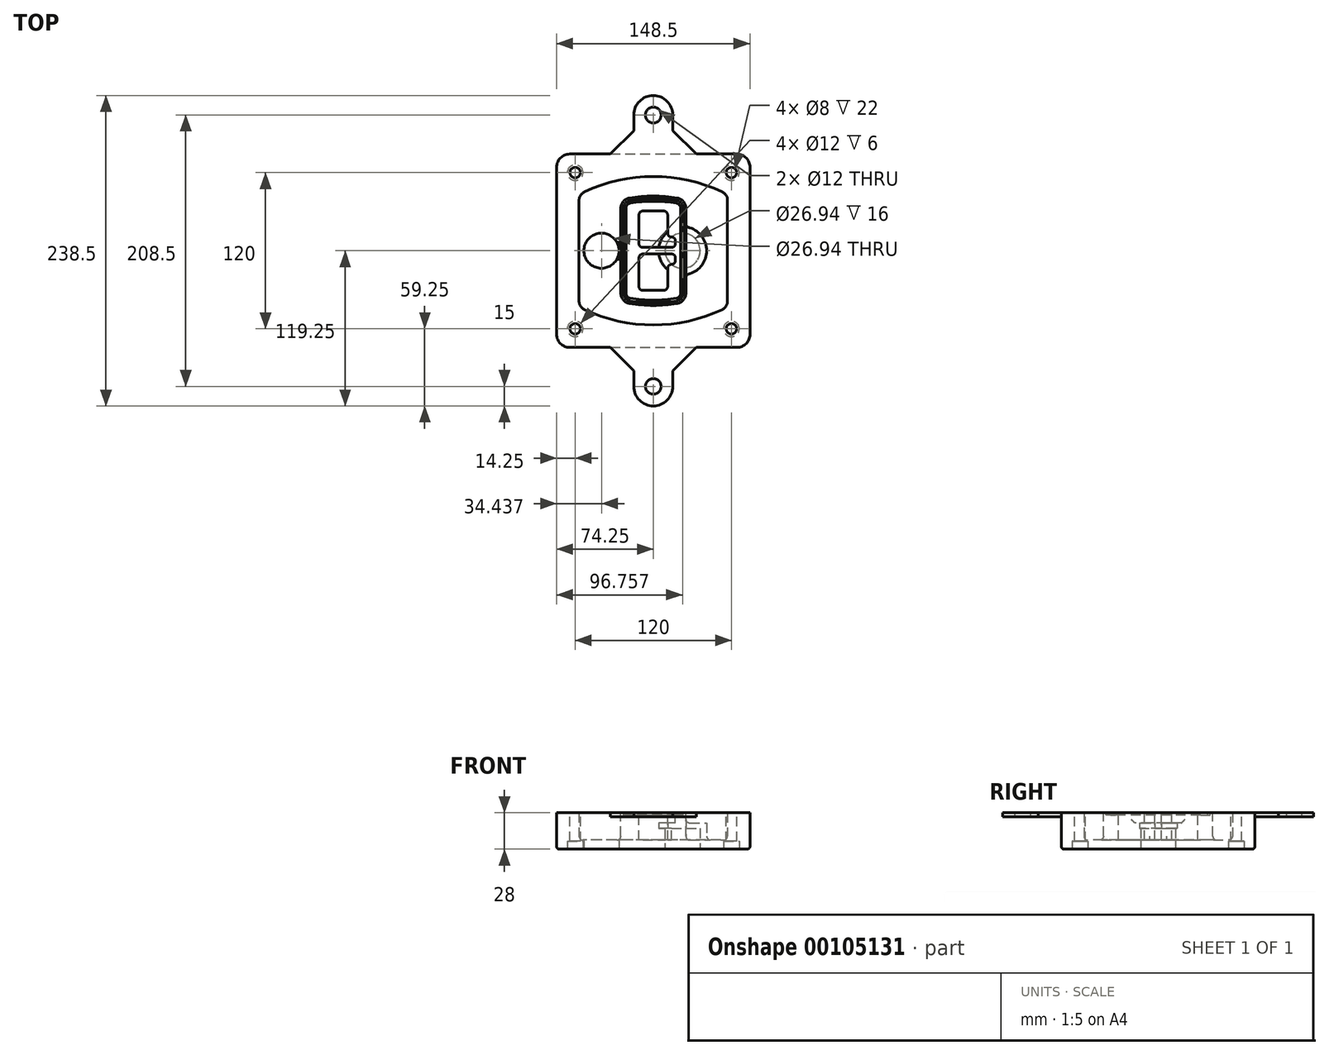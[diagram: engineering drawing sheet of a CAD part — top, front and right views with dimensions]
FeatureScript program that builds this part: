
annotation { "Feature Type Name" : "Feature", "Feature Type Description" : "" }
export const myFeature = defineFeature(function(context is Context, id is Id, definition is map)
    precondition{}
    {
        {
            var Q0;
            Q0=qCreatedBy(makeId("Top.planeOp"),FACE);
            var sketch = newSketch(context, id + "F0", { "sketchPlane" : qUnion([Q0])});
            skPoint(sketch, "E0.rect.middle", {"position": v(0, 0) * mm});
            skLineSegment(sketch, "E1.bottom", {"start": v(-64.25, -74.25) * mm, "end": v(64.25, -74.25) * mm});
            skLineSegment(sketch, "E1.top", {"start": v(-64.25, 74.25) * mm, "end": v(64.25, 74.25) * mm});
            skLineSegment(sketch, "E1.left", {"start": v(-74.25, -64.25) * mm, "end": v(-74.25, 64.25) * mm});
            skLineSegment(sketch, "E1.right", {"start": v(74.25, -64.25) * mm, "end": v(74.25, 64.25) * mm});
            skLineSegment(sketch, "E2", {"start": v(-74.25, 74.25) * mm, "end": v(74.25, -74.25) * mm, "construction": true});
            skLineSegment(sketch, "E3", {"start": v(74.25, 74.25) * mm, "end": v(-74.25, -74.25) * mm, "construction": true});
            skCircle(sketch, "E4", {"center": v(-60, 60) * mm, "radius": 4 * mm});
            skCircle(sketch, "E5", {"center": v(60, 60) * mm, "radius": 4 * mm});
            skCircle(sketch, "E6", {"center": v(60, -60) * mm, "radius": 4 * mm});
            skCircle(sketch, "E7", {"center": v(-60, -60) * mm, "radius": 4 * mm});
            skLineSegment(sketch, "E8", {"start": v(-60, 60) * mm, "end": v(60, 60) * mm, "construction": true});
            skLineSegment(sketch, "E9", {"start": v(60, 60) * mm, "end": v(60, -60) * mm, "construction": true});
            skLineSegment(sketch, "E10", {"start": v(60, -60) * mm, "end": v(-60, -60) * mm, "construction": true});
            skLineSegment(sketch, "E11", {"start": v(-60, -60) * mm, "end": v(-60, 60) * mm, "construction": true});
            skLineSegment(sketch, "E12", {"start": v(-60, 38.83) * mm, "end": v(-60, -38.83) * mm});
            skLineSegment(sketch, "E13", {"start": v(60, 38.83) * mm, "end": v(60, -38.83) * mm});
            skArc(sketch, "E14", {"start": v(54.26, 47.88) * mm, "mid": v(0, 60) * mm, "end": v(-54.26, 47.88) * mm});
            skArc(sketch, "E15", {"start": v(-54.26, -47.88) * mm, "mid": v(0, -60) * mm, "end": v(54.26, -47.88) * mm});
            skLineSegment(sketch, "E16", {"start": v(-60, 0) * mm, "end": v(60, 0) * mm, "construction": true});
            skPoint(sketch, "E17.visualSharp", {"position": v(-60, -45) * mm});
            skArc(sketch, "E17.filletArc", {"start": v(-60, -38.83) * mm, "mid": v(-58.44, -44.2) * mm, "end": v(-54.26, -47.88) * mm});
            skPoint(sketch, "E18.visualSharp", {"position": v(-60, 45) * mm});
            skArc(sketch, "E18.filletArc", {"start": v(-54.26, 47.88) * mm, "mid": v(-58.44, 44.2) * mm, "end": v(-60, 38.83) * mm});
            skPoint(sketch, "E19.visualSharp", {"position": v(60, 45) * mm});
            skArc(sketch, "E19.filletArc", {"start": v(60, 38.83) * mm, "mid": v(58.44, 44.2) * mm, "end": v(54.26, 47.88) * mm});
            skPoint(sketch, "E20.visualSharp", {"position": v(60, -45) * mm});
            skArc(sketch, "E20.filletArc", {"start": v(54.26, -47.88) * mm, "mid": v(58.44, -44.2) * mm, "end": v(60, -38.83) * mm});
            skPoint(sketch, "E21.visualSharp", {"position": v(-74.25, 74.25) * mm});
            skArc(sketch, "E21.filletArc", {"start": v(-64.25, 74.25) * mm, "mid": v(-71.32, 71.32) * mm, "end": v(-74.25, 64.25) * mm});
            skPoint(sketch, "E22.visualSharp", {"position": v(74.25, 74.25) * mm});
            skArc(sketch, "E22.filletArc", {"start": v(74.25, 64.25) * mm, "mid": v(71.32, 71.32) * mm, "end": v(64.25, 74.25) * mm});
            skPoint(sketch, "E23.visualSharp", {"position": v(74.25, -74.25) * mm});
            skArc(sketch, "E23.filletArc", {"start": v(64.25, -74.25) * mm, "mid": v(71.32, -71.32) * mm, "end": v(74.25, -64.25) * mm});
            skPoint(sketch, "E24.visualSharp", {"position": v(-74.25, -74.25) * mm});
            skArc(sketch, "E24.filletArc", {"start": v(-74.25, -64.25) * mm, "mid": v(-71.32, -71.32) * mm, "end": v(-64.25, -74.25) * mm});
            skArc(sketch, "E25.0", {"start": v(57, 38.83) * mm, "mid": v(55.9, 42.58) * mm, "end": v(52.98, 45.17) * mm});
            skLineSegment(sketch, "E25.1", {"start": v(57, 38.83) * mm, "end": v(57, -38.83) * mm});
            skArc(sketch, "E25.2", {"start": v(52.98, -45.17) * mm, "mid": v(55.9, -42.58) * mm, "end": v(57, -38.83) * mm});
            skArc(sketch, "E25.3", {"start": v(-52.98, -45.17) * mm, "mid": v(0, -57) * mm, "end": v(52.98, -45.17) * mm});
            skArc(sketch, "E25.4", {"start": v(-57, -38.83) * mm, "mid": v(-55.9, -42.58) * mm, "end": v(-52.98, -45.17) * mm});
            skArc(sketch, "E25.5", {"start": v(52.98, 45.17) * mm, "mid": v(0, 57) * mm, "end": v(-52.98, 45.17) * mm});
            skLineSegment(sketch, "E25.6", {"start": v(-57, 38.83) * mm, "end": v(-57, -38.83) * mm});
            skArc(sketch, "E25.7", {"start": v(-52.98, 45.17) * mm, "mid": v(-55.9, 42.58) * mm, "end": v(-57, 38.83) * mm});
            skArc(sketch, "E26.0", {"start": v(-55.96, 51.5) * mm, "mid": v(-61.82, 46.33) * mm, "end": v(-64, 38.83) * mm});
            skArc(sketch, "E26.1", {"start": v(55.96, 51.5) * mm, "mid": v(0, 64) * mm, "end": v(-55.96, 51.5) * mm});
            skArc(sketch, "E26.2", {"start": v(64, 38.83) * mm, "mid": v(61.82, 46.33) * mm, "end": v(55.96, 51.5) * mm});
            skLineSegment(sketch, "E26.3", {"start": v(64, 38.83) * mm, "end": v(64, -38.83) * mm});
            skArc(sketch, "E26.4", {"start": v(55.96, -51.5) * mm, "mid": v(61.82, -46.33) * mm, "end": v(64, -38.83) * mm});
            skLineSegment(sketch, "E26.5", {"start": v(-64, 38.83) * mm, "end": v(-64, -38.83) * mm});
            skArc(sketch, "E26.6", {"start": v(-55.96, -51.5) * mm, "mid": v(0, -64) * mm, "end": v(55.96, -51.5) * mm});
            skArc(sketch, "E26.7", {"start": v(-64, -38.83) * mm, "mid": v(-61.82, -46.33) * mm, "end": v(-55.96, -51.5) * mm});
            skSolve(sketch);
        }
        {
            var Q0;
            Q0=makeQuery(id+"F0.imprint","IMPRINT",FACE,{"disambiguationData":[TD([[makeQuery(id+"F0.imprint","IMPRINT",EDGE,{"derivedFrom":sQuery(id+"F0.wireOp",EDGE,"E1.bottom")}),1.0]])]});
            var Q1;
            Q1=makeQuery(id+"F0.imprint","IMPRINT",FACE,{"disambiguationData":[TD([[makeQuery(id+"F0.imprint","IMPRINT",EDGE,{"derivedFrom":sQuery(id+"F0.wireOp",EDGE,"E12")}),1.0]])]});
            var Q2;
            Q2=makeQuery(id+"F0.imprint","IMPRINT",FACE,{"disambiguationData":[TD([[makeQuery(id+"F0.imprint","IMPRINT",EDGE,{"derivedFrom":sQuery(id+"F0.wireOp",EDGE,"E25.0")}),1.0]])]});
            var Q3;
            Q3=makeQuery(id+"F0.imprint","IMPRINT",FACE,{"disambiguationData":[TD([[makeQuery(id+"F0.imprint","IMPRINT",EDGE,{"derivedFrom":sQuery(id+"F0.wireOp",EDGE,"E12")}),-1.0]])]});
            extrude(context, id + "F1", {"entities" : qUnion([Q0, Q1, Q2, Q3]), "oppositeDirection" : true, "depth" : 25 * mm});
        }
        {
            var Q0;
            Q0=makeQuery(id+"F0.imprint","IMPRINT",FACE,{"disambiguationData":[TD([[makeQuery(id+"F0.imprint","IMPRINT",EDGE,{"derivedFrom":sQuery(id+"F0.wireOp",EDGE,"E12")}),1.0]])]});
            extrude(context, id + "F2", {"entities" : qUnion([Q0]), "operationType" : NewBodyOperationType.ADD, "depth" : 3 * mm});
        }
        {
            var Q0;
            Q0=makeQuery(id+"F0.imprint","IMPRINT",FACE,{"disambiguationData":[TD([[makeQuery(id+"F0.imprint","IMPRINT",EDGE,{"derivedFrom":sQuery(id+"F0.wireOp",EDGE,"E25.0")}),1.0]])]});
            extrude(context, id + "F3", {"entities" : qUnion([Q0]), "operationType" : NewBodyOperationType.REMOVE, "oppositeDirection" : true, "depth" : 18 * mm});
        }
        {
            var Q0;
            Q0=makeQuery(id+"F2.opExtrude","CAP_FACE",FACE,{"disambiguationData":[OSD([sQuery(id+"F0.wireOp",EDGE,"E12"),sQuery(id+"F0.wireOp",EDGE,"E13"),sQuery(id+"F0.wireOp",EDGE,"E14"),sQuery(id+"F0.wireOp",EDGE,"E15"),sQuery(id+"F0.wireOp",EDGE,"E17.filletArc"),sQuery(id+"F0.wireOp",EDGE,"E18.filletArc"),sQuery(id+"F0.wireOp",EDGE,"E19.filletArc"),sQuery(id+"F0.wireOp",EDGE,"E20.filletArc"),sQuery(id+"F0.wireOp",EDGE,"E25.0"),sQuery(id+"F0.wireOp",EDGE,"E25.1"),sQuery(id+"F0.wireOp",EDGE,"E25.2"),sQuery(id+"F0.wireOp",EDGE,"E25.3"),sQuery(id+"F0.wireOp",EDGE,"E25.4"),sQuery(id+"F0.wireOp",EDGE,"E25.5"),sQuery(id+"F0.wireOp",EDGE,"E25.6"),sQuery(id+"F0.wireOp",EDGE,"E25.7")])],"isStart":false});
            var sketch = newSketch(context, id + "F4", { "sketchPlane" : qUnion([Q0])});
            skArc(sketch, "E27.0", {"start": v(-18.34, -40.45) * mm, "mid": v(0, -42) * mm, "end": v(18.34, -40.45) * mm});
            skArc(sketch, "E28.0", {"start": v(18.34, 40.45) * mm, "mid": v(0, 42) * mm, "end": v(-18.34, 40.45) * mm});
            skLineSegment(sketch, "E29", {"start": v(-25, 32.57) * mm, "end": v(-25, -32.57) * mm});
            skLineSegment(sketch, "E30", {"start": v(25, 32.57) * mm, "end": v(25, -32.57) * mm});
            skLineSegment(sketch, "E31", {"start": v(-25, 39.1) * mm, "end": v(25, 39.1) * mm, "construction": true});
            skLineSegment(sketch, "E32", {"start": v(-25, -39.1) * mm, "end": v(25, -39.1) * mm, "construction": true});
            skPoint(sketch, "E33.visualSharp", {"position": v(-25, 39.1) * mm});
            skArc(sketch, "E33.filletArc", {"start": v(-18.34, 40.45) * mm, "mid": v(-23.11, 37.73) * mm, "end": v(-25, 32.57) * mm});
            skPoint(sketch, "E34.visualSharp", {"position": v(25, 39.1) * mm});
            skArc(sketch, "E34.filletArc", {"start": v(25, 32.57) * mm, "mid": v(23.11, 37.73) * mm, "end": v(18.34, 40.45) * mm});
            skPoint(sketch, "E35.visualSharp", {"position": v(25, -39.1) * mm});
            skArc(sketch, "E35.filletArc", {"start": v(18.34, -40.45) * mm, "mid": v(23.11, -37.73) * mm, "end": v(25, -32.57) * mm});
            skPoint(sketch, "E36.visualSharp", {"position": v(-25, -39.1) * mm});
            skArc(sketch, "E36.filletArc", {"start": v(-25, -32.57) * mm, "mid": v(-23.11, -37.73) * mm, "end": v(-18.34, -40.45) * mm});
            skArc(sketch, "E37.0", {"start": v(52.98, 45.17) * mm, "mid": v(0, 57) * mm, "end": v(-52.98, 45.17) * mm});
            skArc(sketch, "E37.1", {"start": v(-52.98, 45.17) * mm, "mid": v(-55.9, 42.58) * mm, "end": v(-57, 38.83) * mm});
            skLineSegment(sketch, "E37.2", {"start": v(-57, 38.83) * mm, "end": v(-57, -38.83) * mm});
            skArc(sketch, "E37.3", {"start": v(-57, -38.83) * mm, "mid": v(-55.9, -42.58) * mm, "end": v(-52.98, -45.17) * mm});
            skArc(sketch, "E37.4", {"start": v(-52.98, -45.17) * mm, "mid": v(0, -57) * mm, "end": v(52.98, -45.17) * mm});
            skArc(sketch, "E37.5", {"start": v(52.98, -45.17) * mm, "mid": v(55.9, -42.58) * mm, "end": v(57, -38.83) * mm});
            skLineSegment(sketch, "E37.6", {"start": v(57, 38.83) * mm, "end": v(57, -38.83) * mm});
            skArc(sketch, "E37.7", {"start": v(57, 38.83) * mm, "mid": v(55.9, 42.58) * mm, "end": v(52.98, 45.17) * mm});
            skLineSegment(sketch, "E38.0", {"start": v(23, 32.57) * mm, "end": v(23, -32.57) * mm});
            skArc(sketch, "E38.1", {"start": v(18, -38.48) * mm, "mid": v(21.58, -36.44) * mm, "end": v(23, -32.57) * mm});
            skArc(sketch, "E38.2", {"start": v(-18, -38.48) * mm, "mid": v(0, -40) * mm, "end": v(18, -38.48) * mm});
            skArc(sketch, "E38.3", {"start": v(-23, -32.57) * mm, "mid": v(-21.58, -36.44) * mm, "end": v(-18, -38.48) * mm});
            skLineSegment(sketch, "E38.4", {"start": v(-23, 32.57) * mm, "end": v(-23, -32.57) * mm});
            skArc(sketch, "E38.5", {"start": v(23, 32.57) * mm, "mid": v(21.58, 36.44) * mm, "end": v(18, 38.48) * mm});
            skArc(sketch, "E38.6", {"start": v(-18, 38.48) * mm, "mid": v(-21.58, 36.44) * mm, "end": v(-23, 32.57) * mm});
            skArc(sketch, "E38.7", {"start": v(18, 38.48) * mm, "mid": v(0, 40) * mm, "end": v(-18, 38.48) * mm});
            skArc(sketch, "E39.0", {"start": v(21, 32.57) * mm, "mid": v(20.06, 35.15) * mm, "end": v(17.67, 36.5) * mm});
            skLineSegment(sketch, "E39.1", {"start": v(21, 32.57) * mm, "end": v(21, -32.57) * mm});
            skArc(sketch, "E39.2", {"start": v(17.67, -36.5) * mm, "mid": v(20.06, -35.15) * mm, "end": v(21, -32.57) * mm});
            skArc(sketch, "E39.3", {"start": v(-17.67, -36.5) * mm, "mid": v(0, -38) * mm, "end": v(17.67, -36.5) * mm});
            skArc(sketch, "E39.4", {"start": v(-21, -32.57) * mm, "mid": v(-20.06, -35.15) * mm, "end": v(-17.67, -36.5) * mm});
            skArc(sketch, "E39.5", {"start": v(17.67, 36.5) * mm, "mid": v(0, 38) * mm, "end": v(-17.67, 36.5) * mm});
            skLineSegment(sketch, "E39.6", {"start": v(-21, 32.57) * mm, "end": v(-21, -32.57) * mm});
            skArc(sketch, "E39.7", {"start": v(-17.67, 36.5) * mm, "mid": v(-20.06, 35.15) * mm, "end": v(-21, 32.57) * mm});
            skLineSegment(sketch, "E40", {"start": v(-25, 0) * mm, "end": v(25, 0) * mm, "construction": true});
            skLineSegment(sketch, "E41", {"start": v(-11, 5.5) * mm, "end": v(-11, 27.5) * mm});
            skLineSegment(sketch, "E42", {"start": v(-8, 30.5) * mm, "end": v(8, 30.5) * mm});
            skLineSegment(sketch, "E43", {"start": v(11, 27.5) * mm, "end": v(11, 13.5) * mm});
            skLineSegment(sketch, "E44", {"start": v(14, 10.5) * mm, "end": v(14, 10.5) * mm});
            skLineSegment(sketch, "E45", {"start": v(17, 7.5) * mm, "end": v(17, 5.5) * mm});
            skLineSegment(sketch, "E46", {"start": v(14, 2.5) * mm, "end": v(-8, 2.5) * mm});
            skPoint(sketch, "E47.visualSharp", {"position": v(-11, 30.5) * mm});
            skArc(sketch, "E47.filletArc", {"start": v(-8, 30.5) * mm, "mid": v(-10.12, 29.62) * mm, "end": v(-11, 27.5) * mm});
            skPoint(sketch, "E48.visualSharp", {"position": v(11, 30.5) * mm});
            skArc(sketch, "E48.filletArc", {"start": v(11, 27.5) * mm, "mid": v(10.12, 29.62) * mm, "end": v(8, 30.5) * mm});
            skPoint(sketch, "E49.visualSharp", {"position": v(11, 10.5) * mm});
            skArc(sketch, "E49.filletArc", {"start": v(11, 13.5) * mm, "mid": v(11.88, 11.38) * mm, "end": v(14, 10.5) * mm});
            skPoint(sketch, "E50.visualSharp", {"position": v(17, 10.5) * mm});
            skArc(sketch, "E50.filletArc", {"start": v(17, 7.5) * mm, "mid": v(16.12, 9.62) * mm, "end": v(14, 10.5) * mm});
            skPoint(sketch, "E51.visualSharp", {"position": v(17, 2.5) * mm});
            skArc(sketch, "E51.filletArc", {"start": v(14, 2.5) * mm, "mid": v(16.12, 3.38) * mm, "end": v(17, 5.5) * mm});
            skPoint(sketch, "E52.visualSharp", {"position": v(-11, 2.5) * mm});
            skArc(sketch, "E52.filletArc", {"start": v(-11, 5.5) * mm, "mid": v(-10.12, 3.38) * mm, "end": v(-8, 2.5) * mm});
            skLineSegment(sketch, "E53.0.MirrorCS", {"start": v(14, -2.5) * mm, "end": v(-8, -2.5) * mm});
            skArc(sketch, "E54.0.MirrorCS", {"start": v(-11, -5.5) * mm, "mid": v(-10.12, -3.38) * mm, "end": v(-8, -2.5) * mm});
            skLineSegment(sketch, "E55.0.MirrorCS", {"start": v(-11, -5.5) * mm, "end": v(-11, -27.5) * mm});
            skArc(sketch, "E56.0.MirrorCS", {"start": v(-8, -30.5) * mm, "mid": v(-10.12, -29.62) * mm, "end": v(-11, -27.5) * mm});
            skLineSegment(sketch, "E57.0.MirrorCS", {"start": v(-8, -30.5) * mm, "end": v(8, -30.5) * mm});
            skArc(sketch, "E58.0.MirrorCS", {"start": v(11, -27.5) * mm, "mid": v(10.12, -29.62) * mm, "end": v(8, -30.5) * mm});
            skLineSegment(sketch, "E59.0.MirrorCS", {"start": v(11, -27.5) * mm, "end": v(11, -13.5) * mm});
            skArc(sketch, "E60.0.MirrorCS", {"start": v(11, -13.5) * mm, "mid": v(11.88, -11.38) * mm, "end": v(14, -10.5) * mm});
            skArc(sketch, "E61.0.MirrorCS", {"start": v(17, -7.5) * mm, "mid": v(16.12, -9.62) * mm, "end": v(14, -10.5) * mm});
            skLineSegment(sketch, "E62.0.MirrorCS", {"start": v(17, -7.5) * mm, "end": v(17, -5.5) * mm});
            skArc(sketch, "E63.0.MirrorCS", {"start": v(14, -2.5) * mm, "mid": v(16.12, -3.38) * mm, "end": v(17, -5.5) * mm});
            skSolve(sketch);
        }
        {
            var Q0;
            Q0=makeQuery(id+"F4.imprint","IMPRINT",FACE,{"disambiguationData":[TD([[makeQuery(id+"F4.imprint","IMPRINT",EDGE,{"derivedFrom":sQuery(id+"F4.wireOp",EDGE,"E27.0")}),1.0]])]});
            var Q1;
            Q1=makeQuery(id+"F4.imprint","IMPRINT",FACE,{"disambiguationData":[TD([[makeQuery(id+"F4.imprint","IMPRINT",EDGE,{"derivedFrom":sQuery(id+"F4.wireOp",EDGE,"E38.0")}),-1.0]])]});
            var Q2;
            Q2=makeQuery(id+"F4.imprint","IMPRINT",FACE,{"disambiguationData":[TD([[makeQuery(id+"F4.imprint","IMPRINT",EDGE,{"derivedFrom":sQuery(id+"F4.wireOp",EDGE,"E39.0")}),1.0]])]});
            extrude(context, id + "F5", {"entities" : qUnion([Q0, Q1, Q2]), "operationType" : NewBodyOperationType.ADD, "endBound" : BoundingType.UP_TO_NEXT, "oppositeDirection" : true, "depth" : 25 * mm});
        }
        {
            var Q0;
            Q0=makeQuery(id+"F4.imprint","IMPRINT",FACE,{"disambiguationData":[TD([[makeQuery(id+"F4.imprint","IMPRINT",EDGE,{"derivedFrom":sQuery(id+"F4.wireOp",EDGE,"E38.0")}),-1.0]])]});
            extrude(context, id + "F6", {"entities" : qUnion([Q0]), "operationType" : NewBodyOperationType.REMOVE, "oppositeDirection" : true, "depth" : 2 * mm});
        }
        {
            var Q0;
            Q0=makeQuery(id+"F1.opExtrude","CAP_FACE",FACE,{"disambiguationData":[OSD([sQuery(id+"F0.wireOp",EDGE,"E1.bottom"),sQuery(id+"F0.wireOp",EDGE,"E1.top"),sQuery(id+"F0.wireOp",EDGE,"E1.left"),sQuery(id+"F0.wireOp",EDGE,"E1.right"),sQuery(id+"F0.wireOp",EDGE,"E4"),sQuery(id+"F0.wireOp",EDGE,"E5"),sQuery(id+"F0.wireOp",EDGE,"E6"),sQuery(id+"F0.wireOp",EDGE,"E7"),sQuery(id+"F0.wireOp",EDGE,"E21.filletArc"),sQuery(id+"F0.wireOp",EDGE,"E22.filletArc"),sQuery(id+"F0.wireOp",EDGE,"E23.filletArc"),sQuery(id+"F0.wireOp",EDGE,"E24.filletArc")])],"isStart":false});
            var sketch = newSketch(context, id + "F7", { "sketchPlane" : qUnion([Q0])});
            skCircle(sketch, "E64", {"center": v(22.5, 0) * mm, "radius": 13.47 * mm});
            skCircle(sketch, "E65", {"center": v(-39.81, 0) * mm, "radius": 13.47 * mm});
            skLineSegment(sketch, "E66", {"start": v(74.25, 0) * mm, "end": v(-74.25, 0) * mm});
            skCircle(sketch, "E67", {"center": v(22.5, 0) * mm, "radius": 18.47 * mm});
            skCircle(sketch, "E68", {"center": v(60, -60) * mm, "radius": 6 * mm});
            skCircle(sketch, "E69", {"center": v(-60, -60) * mm, "radius": 6 * mm});
            skCircle(sketch, "E70", {"center": v(-60, 60) * mm, "radius": 6 * mm});
            skCircle(sketch, "E71", {"center": v(60, 60) * mm, "radius": 6 * mm});
            skSolve(sketch);
        }
        {
            var Q0;
            {var subQ1=sQuery(id+"F7.wireOp",EDGE,"E66");var subQ4=sQuery(id+"F7.wireOp",EDGE,"E64");var subQ6=makeQuery(id+"F7.imprint","INTERSECT",VERTEX,{"disambiguationData":[OD(0.0)],"derivedFrom":[subQ4,subQ1]});Q0=makeQuery(id+"F7.imprint","IMPRINT",FACE,{"disambiguationData":[TD([[makeQuery(id+"F7.imprint","IMPRINT",EDGE,{"disambiguationData":[TD([[subQ6,-1.0]])],"derivedFrom":subQ4}),-1.0]])]});}
            var Q1;
            {var subQ0=sQuery(id+"F7.wireOp",EDGE,"E66");var subQ1=sQuery(id+"F7.wireOp",EDGE,"E64");var subQ3=makeQuery(id+"F7.imprint","INTERSECT",VERTEX,{"disambiguationData":[OD(0.0)],"derivedFrom":[subQ1,subQ0]});Q1=makeQuery(id+"F7.imprint","IMPRINT",FACE,{"disambiguationData":[TD([[makeQuery(id+"F7.imprint","IMPRINT",EDGE,{"disambiguationData":[TD([[subQ3,-1.0]])],"derivedFrom":subQ1}),1.0]])]});}
            var Q2;
            {var subQ0=sQuery(id+"F7.wireOp",EDGE,"E66");var subQ1=sQuery(id+"F7.wireOp",EDGE,"E64");var subQ3=makeQuery(id+"F7.imprint","INTERSECT",VERTEX,{"disambiguationData":[OD(0.0)],"derivedFrom":[subQ1,subQ0]});Q2=makeQuery(id+"F7.imprint","IMPRINT",FACE,{"disambiguationData":[TD([[makeQuery(id+"F7.imprint","IMPRINT",EDGE,{"disambiguationData":[TD([[subQ3,1.0]])],"derivedFrom":subQ1}),1.0]])]});}
            var Q3;
            {var subQ1=sQuery(id+"F7.wireOp",EDGE,"E66");var subQ4=sQuery(id+"F7.wireOp",EDGE,"E64");var subQ6=makeQuery(id+"F7.imprint","INTERSECT",VERTEX,{"disambiguationData":[OD(0.0)],"derivedFrom":[subQ4,subQ1]});Q3=makeQuery(id+"F7.imprint","IMPRINT",FACE,{"disambiguationData":[TD([[makeQuery(id+"F7.imprint","IMPRINT",EDGE,{"disambiguationData":[TD([[subQ6,1.0]])],"derivedFrom":subQ4}),-1.0]])]});}
            extrude(context, id + "F8", {"entities" : qUnion([Q0, Q1, Q2, Q3]), "operationType" : NewBodyOperationType.ADD, "oppositeDirection" : true, "depth" : 20 * mm});
        }
        {
            var Q0;
            {var subQ0=sQuery(id+"F7.wireOp",EDGE,"E66");var subQ1=sQuery(id+"F7.wireOp",EDGE,"E64");var subQ3=makeQuery(id+"F7.imprint","INTERSECT",VERTEX,{"disambiguationData":[OD(0.0)],"derivedFrom":[subQ1,subQ0]});Q0=makeQuery(id+"F7.imprint","IMPRINT",FACE,{"disambiguationData":[TD([[makeQuery(id+"F7.imprint","IMPRINT",EDGE,{"disambiguationData":[TD([[subQ3,-1.0]])],"derivedFrom":subQ1}),1.0]])]});}
            var Q1;
            {var subQ0=sQuery(id+"F7.wireOp",EDGE,"E66");var subQ1=sQuery(id+"F7.wireOp",EDGE,"E64");var subQ3=makeQuery(id+"F7.imprint","INTERSECT",VERTEX,{"disambiguationData":[OD(0.0)],"derivedFrom":[subQ1,subQ0]});Q1=makeQuery(id+"F7.imprint","IMPRINT",FACE,{"disambiguationData":[TD([[makeQuery(id+"F7.imprint","IMPRINT",EDGE,{"disambiguationData":[TD([[subQ3,1.0]])],"derivedFrom":subQ1}),1.0]])]});}
            extrude(context, id + "F9", {"entities" : qUnion([Q0, Q1]), "operationType" : NewBodyOperationType.REMOVE, "oppositeDirection" : true, "depth" : 16 * mm});
        }
        {
            var Q0;
            {var subQ0=sQuery(id+"F7.wireOp",EDGE,"E66");var subQ1=sQuery(id+"F7.wireOp",EDGE,"E65");var subQ3=makeQuery(id+"F7.imprint","INTERSECT",VERTEX,{"disambiguationData":[OD(0.0)],"derivedFrom":[subQ1,subQ0]});Q0=makeQuery(id+"F7.imprint","IMPRINT",FACE,{"disambiguationData":[TD([[makeQuery(id+"F7.imprint","IMPRINT",EDGE,{"disambiguationData":[TD([[subQ3,-1.0]])],"derivedFrom":subQ1}),1.0]])]});}
            var Q1;
            {var subQ0=sQuery(id+"F7.wireOp",EDGE,"E66");var subQ1=sQuery(id+"F7.wireOp",EDGE,"E65");var subQ3=makeQuery(id+"F7.imprint","INTERSECT",VERTEX,{"disambiguationData":[OD(0.0)],"derivedFrom":[subQ1,subQ0]});Q1=makeQuery(id+"F7.imprint","IMPRINT",FACE,{"disambiguationData":[TD([[makeQuery(id+"F7.imprint","IMPRINT",EDGE,{"disambiguationData":[TD([[subQ3,1.0]])],"derivedFrom":subQ1}),1.0]])]});}
            extrude(context, id + "F10", {"entities" : qUnion([Q0, Q1]), "operationType" : NewBodyOperationType.REMOVE, "oppositeDirection" : true, "depth" : 25 * mm});
        }
        {
            var Q0;
            Q0=makeQuery(id+"F7.imprint","IMPRINT",FACE,{"disambiguationData":[TD([[makeQuery(id+"F7.imprint","IMPRINT",EDGE,{"derivedFrom":sQuery(id+"F7.wireOp",EDGE,"E68")}),1.0]])]});
            var Q1;
            Q1=makeQuery(id+"F7.imprint","IMPRINT",FACE,{"disambiguationData":[TD([[makeQuery(id+"F7.imprint","IMPRINT",EDGE,{"derivedFrom":makeQuery(id+"F1.opExtrude","CAP_EDGE",EDGE,{"disambiguationData":[OSD([sQuery(id+"F0.wireOp",EDGE,"E5")])],"isStart":false})}),-1.0]])]});
            var Q2;
            Q2=makeQuery(id+"F7.imprint","IMPRINT",FACE,{"disambiguationData":[TD([[makeQuery(id+"F7.imprint","IMPRINT",EDGE,{"derivedFrom":sQuery(id+"F7.wireOp",EDGE,"E69")}),1.0]])]});
            var Q3;
            Q3=makeQuery(id+"F7.imprint","IMPRINT",FACE,{"disambiguationData":[TD([[makeQuery(id+"F7.imprint","IMPRINT",EDGE,{"derivedFrom":makeQuery(id+"F1.opExtrude","CAP_EDGE",EDGE,{"disambiguationData":[OSD([sQuery(id+"F0.wireOp",EDGE,"E4")])],"isStart":false})}),-1.0]])]});
            var Q4;
            Q4=makeQuery(id+"F7.imprint","IMPRINT",FACE,{"disambiguationData":[TD([[makeQuery(id+"F7.imprint","IMPRINT",EDGE,{"derivedFrom":sQuery(id+"F7.wireOp",EDGE,"E70")}),1.0]])]});
            var Q5;
            Q5=makeQuery(id+"F7.imprint","IMPRINT",FACE,{"disambiguationData":[TD([[makeQuery(id+"F7.imprint","IMPRINT",EDGE,{"derivedFrom":makeQuery(id+"F1.opExtrude","CAP_EDGE",EDGE,{"disambiguationData":[OSD([sQuery(id+"F0.wireOp",EDGE,"E7")])],"isStart":false})}),-1.0]])]});
            var Q6;
            Q6=makeQuery(id+"F7.imprint","IMPRINT",FACE,{"disambiguationData":[TD([[makeQuery(id+"F7.imprint","IMPRINT",EDGE,{"derivedFrom":sQuery(id+"F7.wireOp",EDGE,"E71")}),1.0]])]});
            var Q7;
            Q7=makeQuery(id+"F7.imprint","IMPRINT",FACE,{"disambiguationData":[TD([[makeQuery(id+"F7.imprint","IMPRINT",EDGE,{"derivedFrom":makeQuery(id+"F1.opExtrude","CAP_EDGE",EDGE,{"disambiguationData":[OSD([sQuery(id+"F0.wireOp",EDGE,"E6")])],"isStart":false})}),-1.0]])]});
            extrude(context, id + "F11", {"entities" : qUnion([Q0, Q1, Q2, Q3, Q4, Q5, Q6, Q7]), "operationType" : NewBodyOperationType.REMOVE, "oppositeDirection" : true, "depth" : 6 * mm});
        }
        {
            var Q0;
            Q0=makeQuery(id+"F9.boolean.opBoolean","COPY",FACE,{"derivedFrom":makeQuery(id+"F9.opExtrude","CAP_FACE",FACE,{"disambiguationData":[OSD([sQuery(id+"F7.wireOp",EDGE,"E64")])],"isStart":false})});
            var sketch = newSketch(context, id + "F12", { "sketchPlane" : qUnion([Q0])});
            skArc(sketch, "E72.0", {"start": v(11, 14.45) * mm, "mid": v(6.45, 9.13) * mm, "end": v(4.2, 2.5) * mm});
            skArc(sketch, "E72.1", {"start": v(4.2, -2.5) * mm, "mid": v(6.45, -9.13) * mm, "end": v(11, -14.45) * mm});
            skLineSegment(sketch, "E73", {"start": v(4.2, -2.5) * mm, "end": v(14, -2.5) * mm});
            skLineSegment(sketch, "E74.0", {"start": v(14, 2.5) * mm, "end": v(4.2, 2.5) * mm});
            skArc(sketch, "E74.1", {"start": v(14, 2.5) * mm, "mid": v(16.12, 3.38) * mm, "end": v(17, 5.5) * mm});
            skLineSegment(sketch, "E74.2", {"start": v(17, 7.5) * mm, "end": v(17, 5.5) * mm});
            skArc(sketch, "E74.3", {"start": v(17, 7.5) * mm, "mid": v(16.12, 9.62) * mm, "end": v(14, 10.5) * mm});
            skArc(sketch, "E74.4", {"start": v(11, 13.5) * mm, "mid": v(11.88, 11.38) * mm, "end": v(14, 10.5) * mm});
            skLineSegment(sketch, "E74.5", {"start": v(11, 14.45) * mm, "end": v(11, 13.5) * mm});
            skLineSegment(sketch, "E74.7", {"start": v(14, -2.5) * mm, "end": v(4.2, -2.5) * mm});
            skArc(sketch, "E74.8", {"start": v(14, -2.5) * mm, "mid": v(16.12, -3.38) * mm, "end": v(17, -5.5) * mm});
            skLineSegment(sketch, "E74.9", {"start": v(17, -7.5) * mm, "end": v(17, -5.5) * mm});
            skArc(sketch, "E74.10", {"start": v(17, -7.5) * mm, "mid": v(16.12, -9.62) * mm, "end": v(14, -10.5) * mm});
            skArc(sketch, "E74.11", {"start": v(11, -13.5) * mm, "mid": v(11.88, -11.38) * mm, "end": v(14, -10.5) * mm});
            skLineSegment(sketch, "E74.12", {"start": v(11, -14.45) * mm, "end": v(11, -13.5) * mm});
            skPoint(sketch, "E75.orphan", {"position": v(11, -27.5) * mm});
            skPoint(sketch, "E76.orphan", {"position": v(-8, -2.5) * mm});
            skPoint(sketch, "E77.orphan", {"position": v(-8, 2.5) * mm});
            skPoint(sketch, "E78.orphan", {"position": v(11, 27.5) * mm});
            skSolve(sketch);
        }
        {
            var Q0;
            {var subQ7=sQuery(id+"F12.wireOp",EDGE,"E72.0");var subQ14=sQuery(id+"F12.wireOp",EDGE,"E72.1");var subQ16=sQuery(id+"F12.wireOp",EDGE,"E74.1");var subQ18=sQuery(id+"F12.wireOp",EDGE,"E74.8");Q0=qUnion([makeQuery(id+"F12.imprint","IMPRINT",FACE,{"disambiguationData":[TD([[makeQuery(id+"F12.imprint","IMPRINT",EDGE,{"derivedFrom":subQ7}),1.0]])]}),makeQuery(id+"F12.imprint","IMPRINT",FACE,{"disambiguationData":[TD([[makeQuery(id+"F12.imprint","IMPRINT",EDGE,{"derivedFrom":subQ14}),1.0]])]}),makeQuery(id+"F12.imprint","IMPRINT",FACE,{"disambiguationData":[TD([[makeQuery(id+"F12.imprint","IMPRINT",EDGE,{"derivedFrom":subQ16}),1.0]])]}),makeQuery(id+"F12.imprint","IMPRINT",FACE,{"disambiguationData":[TD([[makeQuery(id+"F12.imprint","IMPRINT",EDGE,{"derivedFrom":subQ18}),-1.0]])]})]);}
            var Q1;
            Q1=makeQuery(id+"F5.boolean.opBoolean","SPLIT",FACE,{"disambiguationData":[TD([makeQuery(id+"F5.opExtrude","SWEPT_FACE",FACE,{"disambiguationData":[OSD([sQuery(id+"F4.wireOp",EDGE,"E41")])]})])],"derivedFrom":makeQuery(id+"F3.boolean.opBoolean","COPY",FACE,{"derivedFrom":makeQuery(id+"F3.opExtrude","CAP_FACE",FACE,{"disambiguationData":[OSD([sQuery(id+"F0.wireOp",EDGE,"E25.0"),sQuery(id+"F0.wireOp",EDGE,"E25.1"),sQuery(id+"F0.wireOp",EDGE,"E25.2"),sQuery(id+"F0.wireOp",EDGE,"E25.3"),sQuery(id+"F0.wireOp",EDGE,"E25.4"),sQuery(id+"F0.wireOp",EDGE,"E25.5"),sQuery(id+"F0.wireOp",EDGE,"E25.6"),sQuery(id+"F0.wireOp",EDGE,"E25.7")])],"isStart":false})})});
            extrude(context, id + "F13", {"entities" : qUnion([Q0]), "operationType" : NewBodyOperationType.REMOVE, "endBound" : BoundingType.UP_TO_SURFACE, "endBoundEntityFace" : qUnion([Q1]), "depth" : 25 * mm});
        }
        {
            var Q0;
            Q0=makeQuery(id+"F3.boolean.opBoolean","COPY",EDGE,{"derivedFrom":makeQuery(id+"F3.opExtrude","CAP_EDGE",EDGE,{"disambiguationData":[OSD([sQuery(id+"F0.wireOp",EDGE,"E25.6")])],"isStart":false})});
            var Q1;
            Q1=makeQuery(id+"F8.boolean.opBoolean","INTERSECT",EDGE,{"derivedFrom":[makeQuery(id+"F5.opExtrude","SWEPT_FACE",FACE,{"disambiguationData":[OSD([sQuery(id+"F4.wireOp",EDGE,"E30")])]}),makeQuery(id+"F8.opExtrude","CAP_FACE",FACE,{"disambiguationData":[OSD([sQuery(id+"F7.wireOp",EDGE,"E67")])],"isStart":false})]});
            var Q2;
            Q2=makeQuery(id+"F8.boolean.opBoolean","INTERSECT",EDGE,{"disambiguationData":[OD(1.0)],"derivedFrom":[makeQuery(id+"F5.opExtrude","SWEPT_FACE",FACE,{"disambiguationData":[OSD([sQuery(id+"F4.wireOp",EDGE,"E30")])]}),makeQuery(id+"F8.opExtrude","SWEPT_FACE",FACE,{"disambiguationData":[OSD([sQuery(id+"F7.wireOp",EDGE,"E67")])]})]});
            var Q3;
            {var subQ0=sQuery(id+"F4.wireOp",EDGE,"E30");Q3=makeQuery(id+"F8.boolean.opBoolean","SPLIT",EDGE,{"disambiguationData":[TD([makeQuery(id+"F5.opExtrude","SWEPT_FACE",FACE,{"disambiguationData":[OSD([sQuery(id+"F4.wireOp",EDGE,"E35.filletArc")])]})])],"derivedFrom":makeQuery(id+"F5.opExtrude","CAP_EDGE",EDGE,{"disambiguationData":[OSD([subQ0])],"isStart":false})});}
            var Q4;
            {var subQ0=sQuery(id+"F0.wireOp",EDGE,"E25.7");var subQ1=sQuery(id+"F0.wireOp",EDGE,"E25.1");var subQ2=sQuery(id+"F0.wireOp",EDGE,"E25.6");var subQ3=sQuery(id+"F0.wireOp",EDGE,"E25.5");var subQ4=sQuery(id+"F0.wireOp",EDGE,"E25.4");var subQ5=sQuery(id+"F0.wireOp",EDGE,"E25.0");var subQ6=sQuery(id+"F0.wireOp",EDGE,"E25.2");var subQ7=sQuery(id+"F0.wireOp",EDGE,"E25.3");Q4=makeQuery(id+"F8.boolean.opBoolean","INTERSECT",EDGE,{"derivedFrom":[makeQuery(id+"F5.boolean.opBoolean","SPLIT",FACE,{"disambiguationData":[TD([makeQuery(id+"F2.opExtrude","SWEPT_FACE",FACE,{"disambiguationData":[OSD([subQ5])]})])],"derivedFrom":makeQuery(id+"F3.boolean.opBoolean","COPY",FACE,{"derivedFrom":makeQuery(id+"F3.opExtrude","CAP_FACE",FACE,{"disambiguationData":[OSD([subQ5,subQ1,subQ6,subQ7,subQ4,subQ3,subQ2,subQ0])],"isStart":false})})}),makeQuery(id+"F8.opExtrude","SWEPT_FACE",FACE,{"disambiguationData":[OSD([sQuery(id+"F7.wireOp",EDGE,"E67")])]})]});}
            var Q5;
            Q5=makeQuery(id+"F8.boolean.opBoolean","INTERSECT",EDGE,{"disambiguationData":[OD(0.0)],"derivedFrom":[makeQuery(id+"F5.opExtrude","SWEPT_FACE",FACE,{"disambiguationData":[OSD([sQuery(id+"F4.wireOp",EDGE,"E30")])]}),makeQuery(id+"F8.opExtrude","SWEPT_FACE",FACE,{"disambiguationData":[OSD([sQuery(id+"F7.wireOp",EDGE,"E67")])]})]});
            fillet(context, id + "F14", {"entities" : qUnion([Q0, Q1, Q2, Q3, Q4, Q5]), "radius" : 3 * mm, "tangentPropagation" : true, "allowEdgeOverflow" : false});
        }
        {
            var Q0;
            Q0=makeQuery(id+"F1.opExtrude","CAP_EDGE",EDGE,{"disambiguationData":[OSD([sQuery(id+"F0.wireOp",EDGE,"E1.bottom")])],"isStart":false});
            fillet(context, id + "F15", {"entities" : qUnion([Q0]), "radius" : 2 * mm, "tangentPropagation" : true, "allowEdgeOverflow" : false});
        }
        {
            var Q0;
            {var subQ0=sQuery(id+"F0.wireOp",EDGE,"E22.filletArc");var subQ1=sQuery(id+"F0.wireOp",EDGE,"E7");var subQ2=sQuery(id+"F0.wireOp",EDGE,"E6");var subQ3=sQuery(id+"F0.wireOp",EDGE,"E5");var subQ4=sQuery(id+"F0.wireOp",EDGE,"E4");var subQ5=sQuery(id+"F0.wireOp",EDGE,"E1.bottom");var subQ6=sQuery(id+"F0.wireOp",EDGE,"E21.filletArc");var subQ7=sQuery(id+"F0.wireOp",EDGE,"E1.top");var subQ8=sQuery(id+"F0.wireOp",EDGE,"E1.left");var subQ9=sQuery(id+"F0.wireOp",EDGE,"E1.right");var subQ10=sQuery(id+"F0.wireOp",EDGE,"E23.filletArc");var subQ11=sQuery(id+"F0.wireOp",EDGE,"E24.filletArc");Q0=makeQuery(id+"F2.boolean.opBoolean","SPLIT",FACE,{"disambiguationData":[TD([makeQuery(id+"F1.opExtrude","SWEPT_FACE",FACE,{"disambiguationData":[OSD([subQ5])]})])],"derivedFrom":makeQuery(id+"F1.opExtrude","CAP_FACE",FACE,{"disambiguationData":[OSD([subQ5,subQ7,subQ8,subQ9,subQ4,subQ3,subQ2,subQ1,subQ6,subQ0,subQ10,subQ11])],"isStart":true})});}
            var sketch = newSketch(context, id + "F16", { "sketchPlane" : qUnion([Q0])});
            skLineSegment(sketch, "E79", {"start": v(0, 74.25) * mm, "end": v(0, 104.25) * mm, "construction": true});
            skCircle(sketch, "E80", {"center": v(0, 104.25) * mm, "radius": 6 * mm});
            skArc(sketch, "E81", {"start": v(15, 104.25) * mm, "mid": v(0, 119.25) * mm, "end": v(-15, 104.25) * mm});
            skLineSegment(sketch, "E82", {"start": v(-33, 74.25) * mm, "end": v(-15, 92.25) * mm});
            skLineSegment(sketch, "E83", {"start": v(-15, 92.25) * mm, "end": v(-15, 104.25) * mm});
            skLineSegment(sketch, "E84", {"start": v(33, 74.25) * mm, "end": v(15, 92.25) * mm});
            skLineSegment(sketch, "E85", {"start": v(15, 92.25) * mm, "end": v(15, 104.25) * mm});
            skLineSegment(sketch, "E86", {"start": v(-33, 74.25) * mm, "end": v(33, 74.25) * mm});
            skLineSegment(sketch, "E87.MirrorCS", {"start": v(33, -222.75) * mm, "end": v(15, -240.75) * mm});
            skLineSegment(sketch, "E88", {"start": v(74.25, 0) * mm, "end": v(-74.25, 0) * mm, "construction": true});
            skLineSegment(sketch, "E89.MirrorCS", {"start": v(33, -74.25) * mm, "end": v(15, -92.25) * mm});
            skLineSegment(sketch, "E90.MirrorCS", {"start": v(15, -92.25) * mm, "end": v(15, -104.25) * mm});
            skArc(sketch, "E91.MirrorCS", {"start": v(15, -104.25) * mm, "mid": v(0, -119.25) * mm, "end": v(-15, -104.25) * mm});
            skLineSegment(sketch, "E92.MirrorCS", {"start": v(-15, -92.25) * mm, "end": v(-15, -104.25) * mm});
            skLineSegment(sketch, "E93.MirrorCS", {"start": v(-33, -74.25) * mm, "end": v(-15, -92.25) * mm});
            skLineSegment(sketch, "E94.MirrorCS", {"start": v(-33, -74.25) * mm, "end": v(33, -74.25) * mm});
            skCircle(sketch, "E95.MirrorC", {"center": v(0, -104.25) * mm, "radius": 6 * mm});
            skSolve(sketch);
        }
        {
            var Q0;
            Q0=makeQuery(id+"F16.imprint","IMPRINT",FACE,{"disambiguationData":[TD([[makeQuery(id+"F16.imprint","IMPRINT",EDGE,{"derivedFrom":sQuery(id+"F16.wireOp",EDGE,"E89.MirrorCS")}),-1.0]])]});
            var Q1;
            Q1=makeQuery(id+"F16.imprint","IMPRINT",FACE,{"disambiguationData":[TD([[makeQuery(id+"F16.imprint","IMPRINT",EDGE,{"derivedFrom":sQuery(id+"F16.wireOp",EDGE,"E80")}),-1.0]])]});
            var Q2;
            {var subQ4=sQuery(id+"F16.wireOp",EDGE,"E86");Q2=makeQuery(id+"F16.imprint","IMPRINT",FACE,{"disambiguationData":[TD([[makeQuery(id+"F16.imprint","IMPRINT",EDGE,{"derivedFrom":subQ4}),-1.0]])]});}
            var Q3;
            Q3=makeQuery(id+"F2.opExtrude","CAP_FACE",FACE,{"disambiguationData":[OSD([sQuery(id+"F0.wireOp",EDGE,"E12"),sQuery(id+"F0.wireOp",EDGE,"E13"),sQuery(id+"F0.wireOp",EDGE,"E14"),sQuery(id+"F0.wireOp",EDGE,"E15"),sQuery(id+"F0.wireOp",EDGE,"E17.filletArc"),sQuery(id+"F0.wireOp",EDGE,"E18.filletArc"),sQuery(id+"F0.wireOp",EDGE,"E19.filletArc"),sQuery(id+"F0.wireOp",EDGE,"E20.filletArc"),sQuery(id+"F0.wireOp",EDGE,"E25.0"),sQuery(id+"F0.wireOp",EDGE,"E25.1"),sQuery(id+"F0.wireOp",EDGE,"E25.2"),sQuery(id+"F0.wireOp",EDGE,"E25.3"),sQuery(id+"F0.wireOp",EDGE,"E25.4"),sQuery(id+"F0.wireOp",EDGE,"E25.5"),sQuery(id+"F0.wireOp",EDGE,"E25.6"),sQuery(id+"F0.wireOp",EDGE,"E25.7")])],"isStart":false});
            extrude(context, id + "F17", {"entities" : qUnion([Q0, Q1, Q2]), "operationType" : NewBodyOperationType.ADD, "endBound" : BoundingType.UP_TO_SURFACE, "endBoundEntityFace" : qUnion([Q3]), "depth" : 25 * mm});
        }
    });
